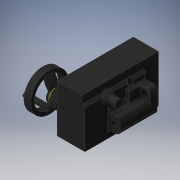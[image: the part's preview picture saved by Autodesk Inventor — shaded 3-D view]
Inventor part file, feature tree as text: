
AUTODESK INVENTOR PART (.ipt)
format: ipt  version: 2016 (Build 200138000, 138)  size: 585,216 bytes
history: native  units: in
note: dims shown in document units (in); Inventor stores cm internally (conversion verified against a paired STEP export)
features: sketch x20, extrude x16, fillet x6, plane x3, loft x2, projected_geometry x2, chamfer x1, other x1
ambient origin geometry x8: Origin, YZ Plane, XZ Plane, XY Plane, X Axis, Y Axis, Z Axis, Center Point
bodies: Solid1 (feature_tree)
feature tree (51):
  extrude  "Extrusion1"  Depth=4.3701in
  extrude  "Extrusion2"  Depth=1.1811in
  extrude  "Extrusion3"  Depth=12.0079in TaperAngle=0.0deg
  extrude  "Extrusion4"  Depth=12.0079in TaperAngle=0.0deg
  extrude  "Extrusion5"  Depth=1.9685in
  extrude  "Extrusion6"  Depth=1.4567in TaperAngle=0.0deg
  extrude  "Extrusion7"  Depth=4.6457in TaperAngle=0.0deg
  fillet  "Fillet2"  Radius=1.7717in
  chamfer  "Chamfer1"  Distance=0.5512in
  fillet  "Fillet3"  Radius=0.7874in
  extrude  "Extrusion8"  Depth=0.5118in TaperAngle=0.0deg
  extrude  "Extrusion9"  Depth=0.315in
  extrude  "Extrusion10"  Depth=0.2559in TaperAngle=0.0deg
  fillet  "Fillet4"  Radius=0.5906in
  extrude  "Extrusion11"  Depth=0.0787in
  extrude  "Extrusion12"  Depth=0.0787in
  sketch  "Sketch14"  dims[d39=0.9449in d40=0.7874in]
  plane  "Work Plane2"
  loft  "Loft1"
  plane  "Work Plane3"
  extrude  "Extrusion13"  Depth=1.1417in
  extrude  "Extrusion15"  Depth=1.7717in
  plane  "Work Plane5"
  sketch  "Sketch22"  dims[d55=3.3071in d56=1.1811in]
  sketch  "Sketch16"  dims[d43=0.2559in d44=0.0in d45=1.7717in]
  loft  "Loft2"
  fillet  "Fillet5"  Radius=0.8268in
  extrude  "Extrusion16"  Depth=1.4173in TaperAngle=0.0deg
  fillet  "Fillet6"  Radius=0.1181in
  fillet  "Fillet7"  Radius=2.7559in
  extrude  "Extrusion17"  Depth=1.1811in
  sketch  "Sketch1"  dims[d0=3.937in d1=4.3701in]
  sketch  "Sketch2"  dims[d2=7.4803in d3=1.1811in]
  sketch  "Sketch3"  dims[d4=5.9843in d5=12.0079in d6=0.0in]
  sketch  "Sketch4"  dims[d7=2.3228in d8=12.0079in d9=0.0in]
  sketch  "Sketch5"  dims[d10=0.7087in d11=1.9685in]
  sketch  "Sketch6"  dims[d12=3.8976in d13=1.4567in d14=0.0in]
  sketch  "Sketch7"  dims[d15=1.5748in d16=4.6457in d17=0.0in d18=1.7717in d19=0.5512in d20=0.0in d21=0.7874in]
  sketch  "Sketch9"  dims[d22=0.7874in d23=0.5118in d24=0.0in]
  sketch  "Sketch10"  dims[d25=2.3622in d26=0.315in]
  sketch  "Sketch11"  dims[d27=0.5906in d28=0.2559in d29=0.0in d31=0.5906in]
  sketch  "Sketch12"  dims[d32=0.5118in d33=0.0787in d34=45.0deg d36=1.1811in]
  sketch  "Sketch13"  dims[d37=1.6142in d38=0.0787in]
  projected_geometry  "Projected Loop1"
  sketch  "Sketch15"  dims[d41=0.9646in d42=1.1417in]
  other  "Edges1"
  sketch  "Sketch18"  dims[d46=1.5748in d47=3.5827in d48=0.8268in d49=0.0in]
  sketch  "Sketch21"  dims[d50=1.2205in d51=1.4173in d52=0.0in d53=0.1181in d54=2.7559in]
  projected_geometry  "Projected Loop4"
  sketch  "Sketch23"  dims[d57=1.1417in d58=0.0in]
  sketch  "Sketch24"  dims[d59=2.2047in d60=0.2756in d61=0.0in d62=0.9449in d63=5.1181in d64=0.0in d65=90.0deg d66=0.0in d67=90.0deg d68=0.6693in d69=2.2047in d71=0.0in d72=90.0deg d75=2.2047in d76=4.7244in d78=0.7874in d79=0.5118in d80=0.2756in d81=0.0in d82=2.7559in d87=5.9843in d88=4.8031in d89=1.063in d90=0.0in d91=1.7717in d92=0.0in d93=90.0deg d94=0.5906in d95=0.7874in d96=2.2047in d97=1.063in d98=0.0in d99=0.0787in d100=0.0787in d101=2.7559in d102=0.0in]
